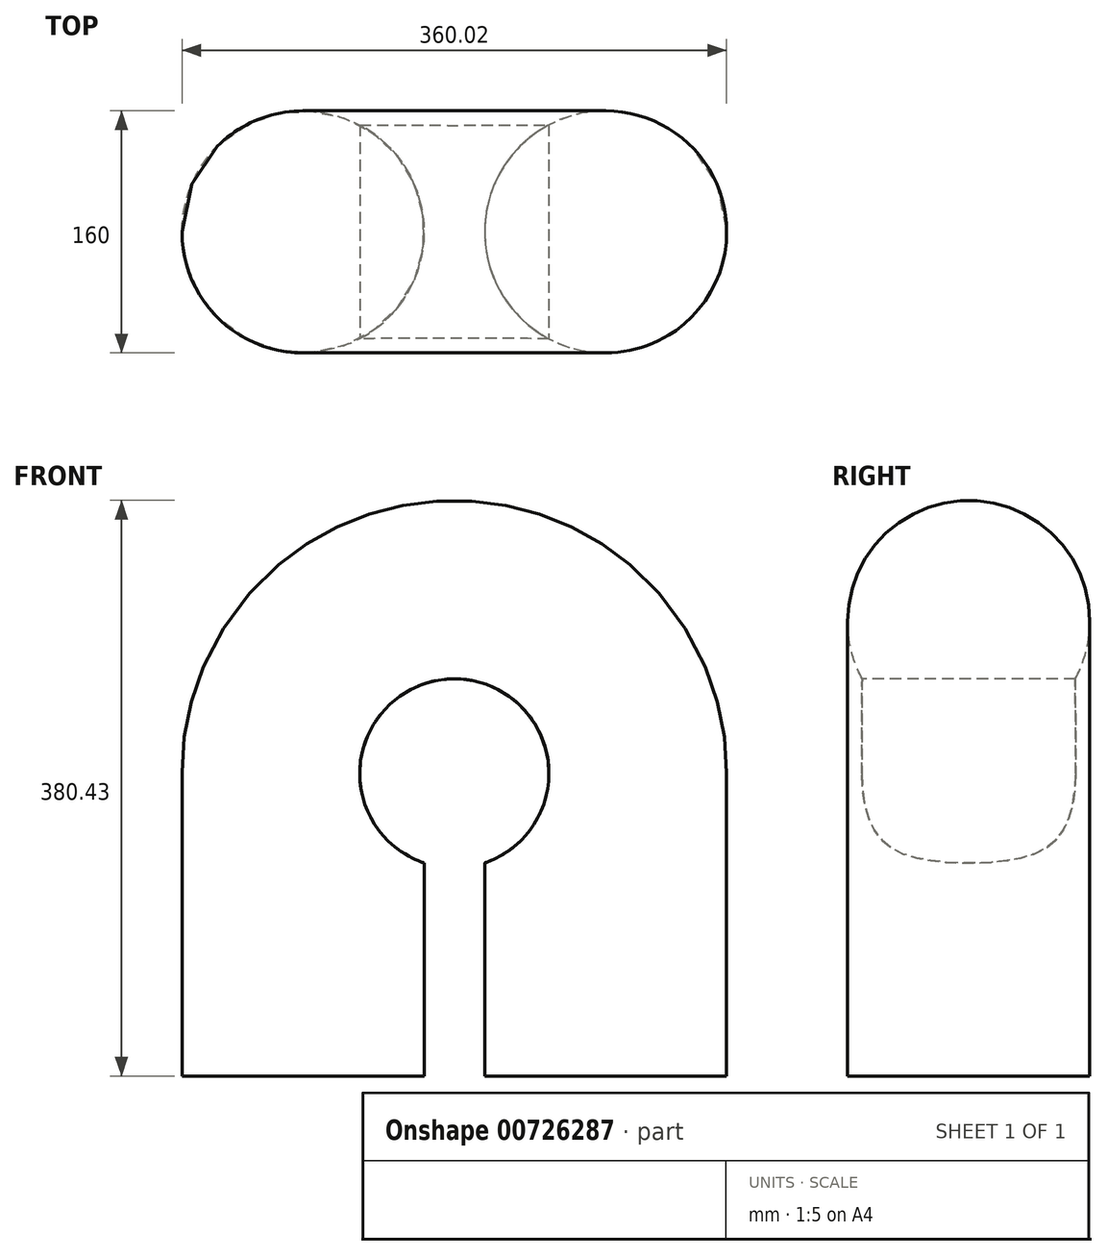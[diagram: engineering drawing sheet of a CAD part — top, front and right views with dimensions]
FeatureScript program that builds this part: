
annotation { "Feature Type Name" : "Feature", "Feature Type Description" : "" }
export const myFeature = defineFeature(function(context is Context, id is Id, definition is map)
    precondition{}
    {
        {
            var Q0;
            Q0=qCreatedBy(makeId("Front.planeOp"),FACE);
            var sketch = newSketch(context, id + "F0", { "sketchPlane" : qUnion([Q0])});
            skLineSegment(sketch, "E0.left", {"start": v(100, -0.86) * mm, "end": v(100, 100) * mm});
            skLineSegment(sketch, "E0.right", {"start": v(-100, 0) * mm, "end": v(-100, 100) * mm});
            skArc(sketch, "E1", {"start": v(100, 100) * mm, "mid": v(0, 200.43) * mm, "end": v(-100, 100) * mm});
            skPoint(sketch, "E1.centerSnap0", {"position": v(0, 100) * mm});
            skLineSegment(sketch, "E2", {"start": v(-100, 0) * mm, "end": v(-100, -100) * mm});
            skLineSegment(sketch, "E3", {"start": v(100, -0.86) * mm, "end": v(100, -100) * mm});
            skSolve(sketch);
        }
        {
            var Q0;
            Q0=qCreatedBy(makeId("Top.planeOp"),FACE);
            var sketch = newSketch(context, id + "F1", { "sketchPlane" : qUnion([Q0])});
            skCircle(sketch, "E4", {"center": v(100, 0) * mm, "radius": 80 * mm});
            skSolve(sketch);
        }
        {
            var Q0;
            Q0=makeQuery(id+"F1.imprint","IMPRINT",FACE,{"disambiguationData":[TD([[makeQuery(id+"F1.imprint","IMPRINT",EDGE,{"derivedFrom":sQuery(id+"F1.wireOp",EDGE,"E4")}),1.0]])]});
            var Q1;
            Q1=sQuery(id+"F0.wireOp",EDGE,"E0.left");
            var Q2;
            Q2=sQuery(id+"F0.wireOp",EDGE,"E1");
            var Q3;
            Q3=sQuery(id+"F0.wireOp",EDGE,"E0.right");
            var Q4;
            Q4=sQuery(id+"F0.wireOp",EDGE,"E3");
            var Q5;
            Q5=sQuery(id+"F0.wireOp",EDGE,"E2");
            sweep(context, id + "F2", {"profiles" : qUnion([Q0]), "path" : qUnion([Q1, Q2, Q3, Q4, Q5])});
        }
        {
            var Q0;
            Q0=qCreatedBy(makeId("Front.planeOp"),FACE);
            var sketch = newSketch(context, id + "F3", { "sketchPlane" : qUnion([Q0])});
            skCircle(sketch, "E5", {"center": v(0, 100) * mm, "radius": 62.5 * mm});
            skSolve(sketch);
        }
        {
            var Q0;
            Q0=qSketchRegion(id+"F3",true);
            extrude(context, id + "F4", {"entities" : qUnion([Q0]), "operationType" : NewBodyOperationType.REMOVE, "oppositeDirection" : true, "depth" : 200 * mm, "offsetDistance" : 25 * mm, "symmetric" : true});
        }
    });
